# Revit family: svetilnik_alfresco_solyaris-6
name_source: partatom
category: Осветительные приборы
revit_build: Autodesk Revit 2016 (Build: 20150714_1515(x64)
units: mm (PartAtom-declared; Revit-internal decimal feet)

## family parameters
Всегда вертикально = Да
Источник света = Нет
На основе рабочей плоскости = Нет
Общий = Нет
При загрузке вырезать с полостями = Нет
Размер круглого соединителя = Использовать диаметр
Тип детали = Нормальный
Точка расчета площади = Нет

## types (2) — shared parameters
ADSK_Единица измерения = шт
ADSK_Классификация нагрузок = Освещение
ADSK_Количество фаз = 2
ADSK_Количество фаз числовое = 2
ADSK_Коэффициент мощности = 0.97
ADSK_Модель = Солярис 6-1
ADSK_Напряжение = 220 В
ADSK_Размер_Ширина = 450 мм
ADSK_Энергоэффективность = 90 лм/Вт
IP Class = IP 54
URL = http://www.allfresco.ru
Блок аварийного питания = Нет
Изготовитель = ALFRESCO
Класс Защиты = 1
Класс пожароопасности = F (светильники предназначены для установки непосредственно на поверхность из нормально воспламеняемых матеоиалов)
Климатическая зона = УХЛ1
Область использования = Ландшафт, коттедж.поселки,микрорайоны,АЗС, автостоянки
Температура эксплуатации = -35 +40
Тип ИС = МГЛ-лампа
Тип КСС = Sym
Тип ПРА = ЭМПРА
Тип продукции = Комплект(Опора освещения+LED светильник)
Цветовая температура = 4000

## per-type parameters (varying)
| type | ADSK_Артикул | ADSK_Масса | ADSK_Наименование | ADSK_Номинальная мощность | ADSK_Полная мощность | ADSK_Размер_Высота | ADSK_Размер_Длина | ADSK_Ток | Полная установленная мощность | Световой поток | Солярис 6-1 | Солярис6-2 |
| Солярис 6_1(ОС) — МГЛ150 G12 | 1105001640 | 40 | Солярис 6_1(ОС) — МГЛ150 G12 св-к Солярис-6 на опоре ОС 3,7 ЧС | 150 Вт | 155 В·А | 4500 мм | 450 мм | 0 А | 155 В·А | 6300 лм | Да | Нет |
| Солярис 6-2(47) — МГЛ150 G12 | 1142000030 | 123 | Солярис 6-2(47) — МГЛ150 G12 св-к Солярис-6 ЧС на опоре OYE 4,0-КР2-47 оц+ЧС | 300 Вт | 309 В·А | 5280 мм | 1790 мм | 1 А | 309 В·А | 13500 лм | Нет | Да |

## geometry (parser evidence)
native form markers: Blend x2
no freeform markers — native parametric forms only
